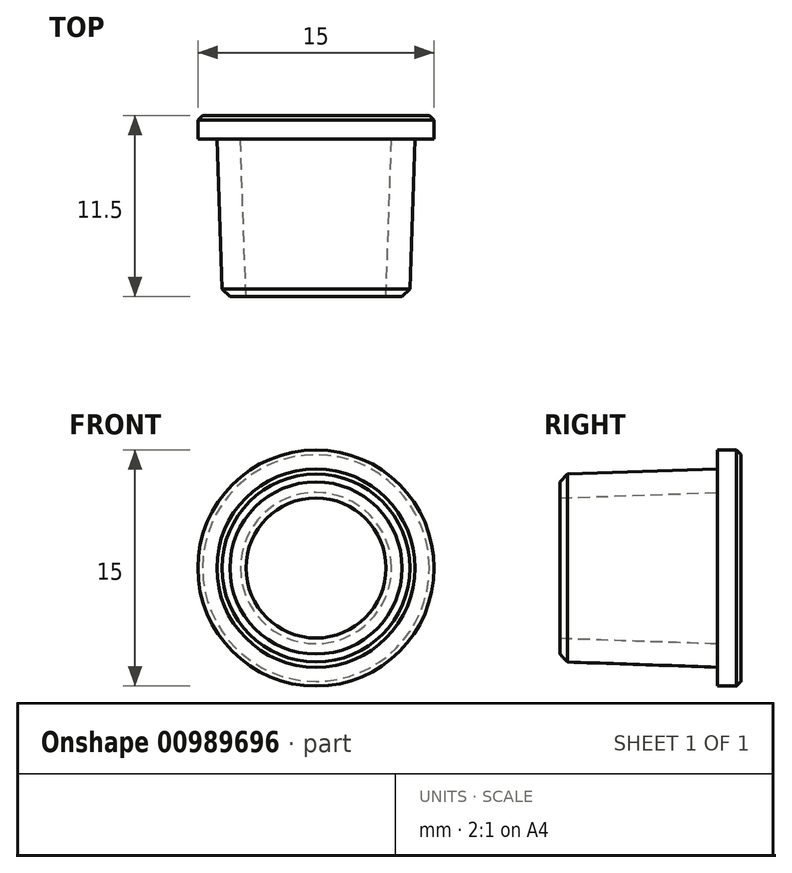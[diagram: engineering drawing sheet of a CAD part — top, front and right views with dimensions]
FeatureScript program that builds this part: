
annotation { "Feature Type Name" : "Feature", "Feature Type Description" : "" }
export const myFeature = defineFeature(function(context is Context, id is Id, definition is map)
    precondition{}
    {
        {
            var Q0;
            Q0=qCreatedBy(makeId("Front.planeOp"),FACE);
            var sketch = newSketch(context, id + "F0", { "sketchPlane" : qUnion([Q0])});
            skCircle(sketch, "E0", {"center": v(0, 0) * mm, "radius": 7.5 * mm});
            skCircle(sketch, "E1", {"center": v(0, 0) * mm, "radius": 6.3 * mm});
            skSolve(sketch);
        }
        {
            var Q0;
            Q0=makeQuery(id+"F0.imprint","IMPRINT",FACE,{"disambiguationData":[TD([[makeQuery(id+"F0.imprint","IMPRINT",EDGE,{"derivedFrom":sQuery(id+"F0.wireOp",EDGE,"E1")}),1.0]])]});
            extrude(context, id + "F1", {"entities" : qUnion([Q0]), "depth" : 10 * mm, "offsetDistance" : 25 * mm, "hasDraft" : true, "draftAngle" : 2 * degree, "draftPullDirection" : true});
        }
        {
            var Q0;
            Q0 = qSketchRegion(id + "F0", true);
            var Q1;
            Q1=makeQuery(id+"F1.opExtrude","CAP_FACE",FACE,{"disambiguationData":[OSD([sQuery(id+"F0.wireOp",EDGE,"E1")])],"isStart":true});
            extrude(context, id + "F2", {"entities" : qUnion([Q0, Q1]), "operationType" : NewBodyOperationType.ADD, "oppositeDirection" : true, "depth" : 1.5 * mm, "offsetDistance" : 25 * mm});
        }
        {
            var Q0;
            Q0=makeQuery(id+"F2.opExtrude","CAP_EDGE",EDGE,{"disambiguationData":[OSD([sQuery(id+"F0.wireOp",EDGE,"E0")])],"isStart":false});
            chamfer(context, id + "F3", {"entities" : qUnion([Q0]), "width" : 0.3 * mm, "tangentPropagation" : true});
        }
        {
            var Q0;
            Q0=makeQuery(id+"F1.opExtrude","CAP_FACE",FACE,{"disambiguationData":[OSD([sQuery(id+"F0.wireOp",EDGE,"E1")])],"isStart":false});
            shell(context, id + "F4", {"entities" : qUnion([Q0]), "thickness" : 1.5 * mm});
        }
        {
            var Q0;
            Q0=makeQuery(id+"F1.opExtrude","CAP_EDGE",EDGE,{"disambiguationData":[OSD([sQuery(id+"F0.wireOp",EDGE,"E1")])],"isStart":false});
            chamfer(context, id + "F5", {"entities" : qUnion([Q0]), "width" : 0.5 * mm, "tangentPropagation" : true});
        }
    });
